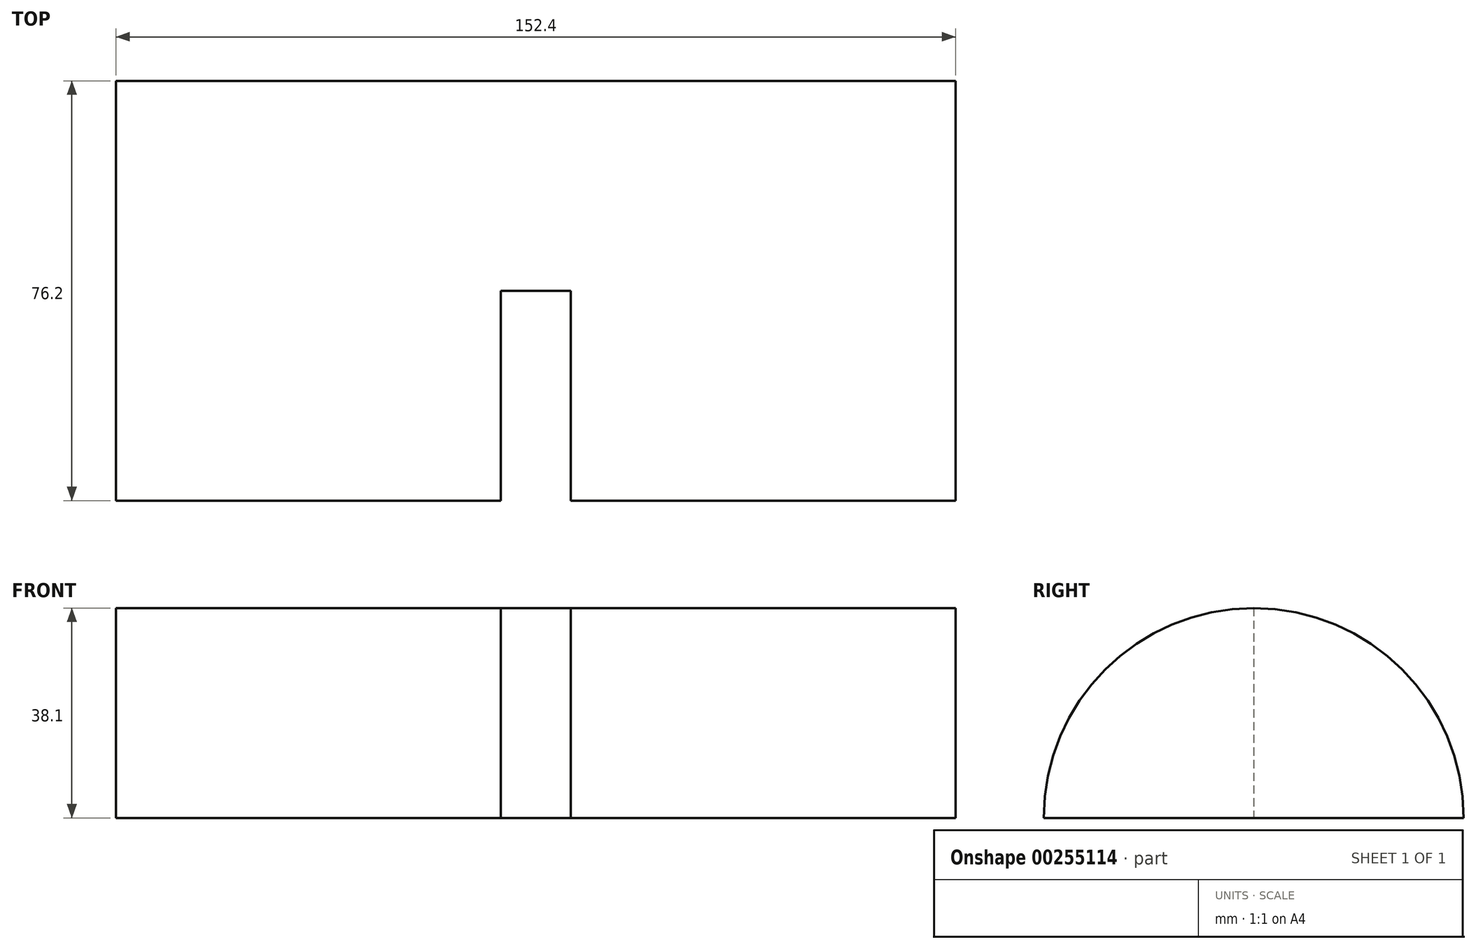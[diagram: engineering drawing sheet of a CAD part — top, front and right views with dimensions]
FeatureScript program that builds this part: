
annotation { "Feature Type Name" : "Feature", "Feature Type Description" : "" }
export const myFeature = defineFeature(function(context is Context, id is Id, definition is map)
    precondition{}
    {
        {
            var Q0;
            Q0=qCreatedBy(makeId("Right.planeOp"),FACE);
            var sketch = newSketch(context, id + "F0", { "sketchPlane" : qUnion([Q0])});
            skArc(sketch, "E0", {"start": v(38.1, 0) * mm, "mid": v(0, 38.1) * mm, "end": v(-38.1, 0) * mm});
            skLineSegment(sketch, "E1", {"start": v(-38.1, 0) * mm, "end": v(38.1, 0) * mm});
            skSolve(sketch);
        }
        {
            var Q0;
            Q0 = qSketchRegion(id + "F0", true);
            extrude(context, id + "F1", {"entities" : qUnion([Q0]), "oppositeDirection" : true, "depth" : 152.4 * mm});
        }
        {
            var Q0;
            Q0=makeQuery(id+"F1.opExtrude","SWEPT_FACE",FACE,{"disambiguationData":[OSD([sQuery(id+"F0.wireOp",EDGE,"E1")])]});
            var sketch = newSketch(context, id + "F2", { "sketchPlane" : qUnion([Q0])});
            skLineSegment(sketch, "E2.0", {"start": v(-152.4, 38.1) * mm, "end": v(0, 38.1) * mm});
            skLineSegment(sketch, "E3.0", {"start": v(-152.4, 38.1) * mm, "end": v(-152.4, -38.1) * mm});
            skLineSegment(sketch, "E4.0", {"start": v(-152.4, -38.1) * mm, "end": v(0, -38.1) * mm});
            skLineSegment(sketch, "E5.0", {"start": v(0, 38.1) * mm, "end": v(0, -38.1) * mm});
            skLineSegment(sketch, "E6.0", {"start": v(-69.85, 38.1) * mm, "end": v(-69.85, 0) * mm});
            skLineSegment(sketch, "E7.0", {"start": v(-82.55, 38.1) * mm, "end": v(-82.55, 0) * mm});
            skLineSegment(sketch, "E8", {"start": v(-82.55, 0) * mm, "end": v(-69.85, 0) * mm});
            skSolve(sketch);
        }
        {
            var Q0;
            {var subQ0=sQuery(id+"F2.wireOp",EDGE,"E6.0");Q0=makeQuery(id+"F2.imprint","IMPRINT",FACE,{"disambiguationData":[TD([[makeQuery(id+"F2.imprint","IMPRINT",EDGE,{"derivedFrom":subQ0}),-1.0]])]});}
            extrude(context, id + "F3", {"entities" : qUnion([Q0]), "operationType" : NewBodyOperationType.REMOVE, "endBound" : BoundingType.THROUGH_ALL, "oppositeDirection" : true, "depth" : 25.4 * mm});
        }
    });
